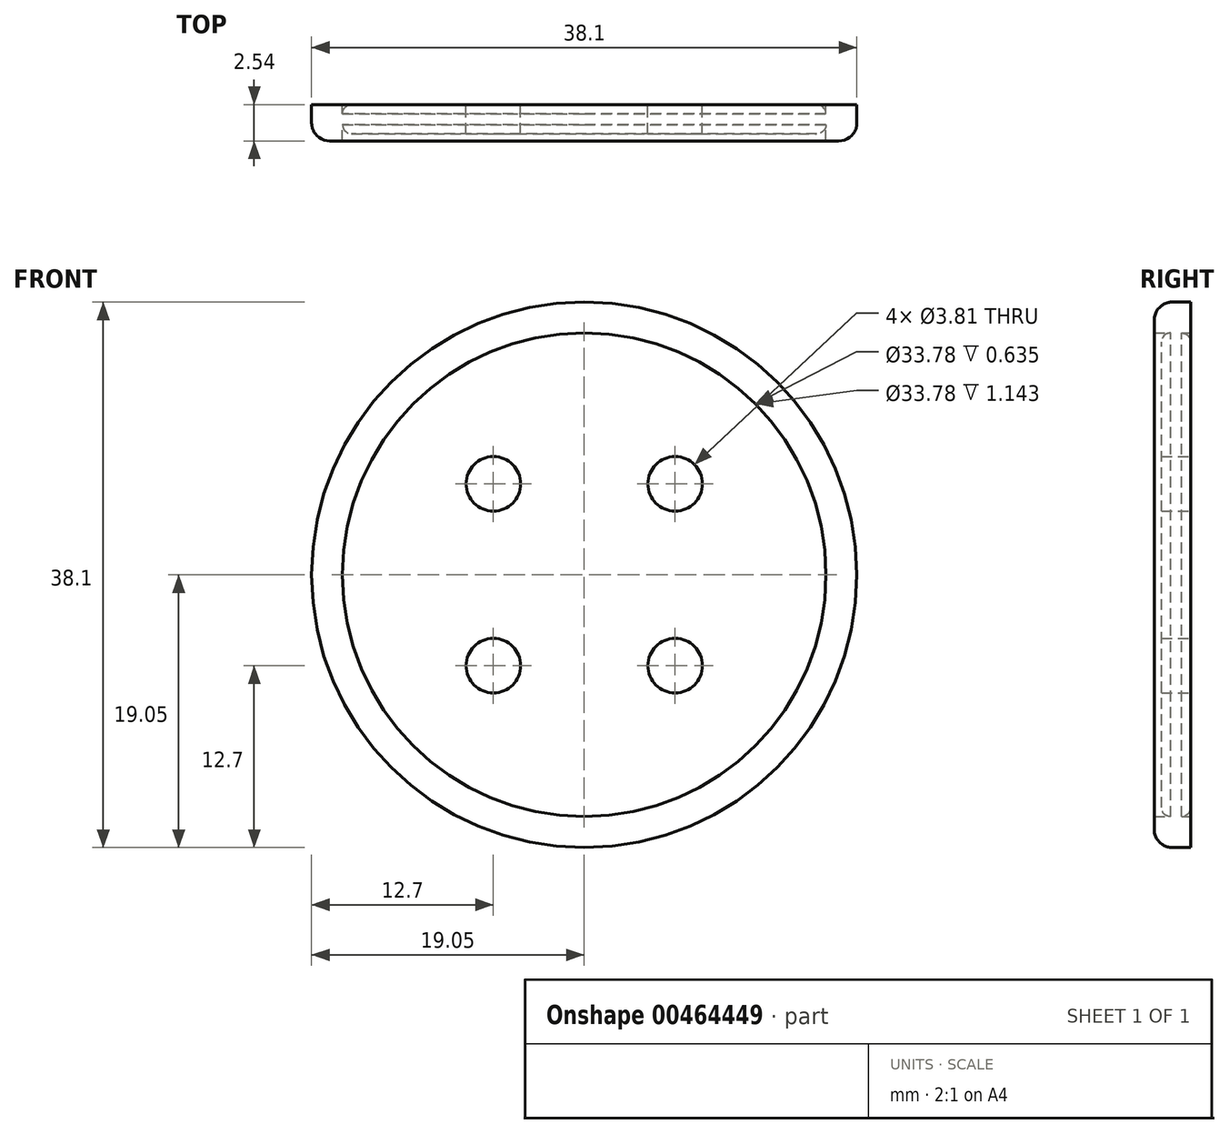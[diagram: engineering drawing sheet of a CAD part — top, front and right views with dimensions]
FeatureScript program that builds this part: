
annotation { "Feature Type Name" : "Feature", "Feature Type Description" : "" }
export const myFeature = defineFeature(function(context is Context, id is Id, definition is map)
    precondition{}
    {
        {
            var Q0;
            Q0=qCreatedBy(makeId("Front.planeOp"),FACE);
            var sketch = newSketch(context, id + "F0", { "sketchPlane" : qUnion([Q0])});
            skCircle(sketch, "E0", {"center": v(0, 0) * mm, "radius": 19.05 * mm});
            skCircle(sketch, "E1", {"center": v(0, 0) * mm, "radius": 16.9 * mm});
            skCircle(sketch, "E2", {"center": v(-6.35, 6.35) * mm, "radius": 1.9 * mm});
            skCircle(sketch, "E3", {"center": v(6.35, -6.35) * mm, "radius": 1.9 * mm});
            skCircle(sketch, "E4", {"center": v(6.35, 6.35) * mm, "radius": 1.9 * mm});
            skCircle(sketch, "E5", {"center": v(-6.35, -6.35) * mm, "radius": 1.9 * mm});
            skSolve(sketch);
        }
        {
            var Q0;
            Q0=makeQuery(id+"F0.imprint","IMPRINT",FACE,{"disambiguationData":[TD([[makeQuery(id+"F0.imprint","IMPRINT",EDGE,{"derivedFrom":sQuery(id+"F0.wireOp",EDGE,"E1")}),1.0]])]});
            extrude(context, id + "F1", {"entities" : qUnion([Q0]), "depth" : 2.03 * mm});
        }
        {
            var Q0;
            Q0=makeQuery(id+"F1.opExtrude","CAP_EDGE",EDGE,{"disambiguationData":[OSD([sQuery(id+"F0.wireOp",EDGE,"E1")])],"isStart":false});
            var Q1;
            Q1=makeQuery(id+"F1.opExtrude","CAP_EDGE",EDGE,{"disambiguationData":[OSD([sQuery(id+"F0.wireOp",EDGE,"E1")])],"isStart":true});
            fillet(context, id + "F2", {"entities" : qUnion([Q0, Q1]), "radius" : 0.64 * mm, "tangentPropagation" : true, "allowEdgeOverflow" : false});
        }
        {
            var Q0;
            Q0=makeQuery(id+"F0.imprint","IMPRINT",FACE,{"disambiguationData":[TD([[makeQuery(id+"F0.imprint","IMPRINT",EDGE,{"derivedFrom":sQuery(id+"F0.wireOp",EDGE,"E0")}),1.0]])]});
            extrude(context, id + "F3", {"entities" : qUnion([Q0]), "operationType" : NewBodyOperationType.ADD, "depth" : 2.54 * mm});
        }
        {
            var Q0;
            Q0=makeQuery(id+"F3.opExtrude","CAP_EDGE",EDGE,{"disambiguationData":[OSD([sQuery(id+"F0.wireOp",EDGE,"E0")])],"isStart":false});
            fillet(context, id + "F4", {"entities" : qUnion([Q0]), "radius" : 1.27 * mm, "tangentPropagation" : true, "allowEdgeOverflow" : false});
        }
    });
